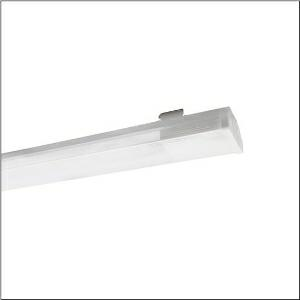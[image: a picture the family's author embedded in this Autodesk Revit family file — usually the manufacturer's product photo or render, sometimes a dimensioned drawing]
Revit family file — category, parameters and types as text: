
# Revit family: modario_r__31_gen_2_53bm8127u4l3d2_2c8d
name_source: partatom
category: Lighting Fixtures
units: mm (PartAtom-declared; Revit-internal decimal feet)

## family parameters
Cut with Voids When Loaded = No
Host = Face
Light Source = No
Part Type = Normal
Room Calculation Point = No
Round Connector Dimension = Use Diameter
Shared = No

## types (1)
- Modario® 31 Gen.2 (1 x LED, 23600 lm, 126 W, 4000K)
    Apparent Load = 126 VA
    CIE Flux Codes = 47 80 95 93 100
    Color Rendering = 80
    Color Temperature = 4000K
    Default Elevation = 1800 mm
    Description = Modario® 31 Gen.2, luminaire insert, of sheet steel, coil coated, white, length: 2.392mm, width: 81mm, height: 82mm, 8x system unit, system units: 299mm, LED rated luminous flux: 23.600lm, light colour: 840, control gear: ON/OFF, with plug, 3-pole, with phase selection, mains connection: 220..240V, AC, 50/60Hz, rated input power: 126W, through-wiring accessed according to module size, primary optical cover: cover, of PMMA, light emission: direct distribution, primary light characteristic: symmetric, protection rating (complete): IP20, protection rating (LED compartment): IP50, insulation class (complete): insulation class I (protective earthing), certification: CE, ENEC, VDE, UKCA, impact resistance: IK03, permissible ambient temperature for indoor applications: -40..+35°C, corresponds to IFS (International Featured Standards) requirements for safety and quality in the food industry, reducing of maximum allowable ambient temperature of 5°C with ceiling mounting, packaging unit: 1 piece
    Height = 92 mm
    Lamp = 1 x LED
    Lamp Light Flux = 23600 lm
    Lamp Power = 126 W
    Lamp count = 1
    Length = 2392 mm
    Luminous efficacy = 187 lm/W
    Manufacturer = Siteco
    ModVariant = No
    Model = 53BM8127U4L3D2
    Mounting Place = Ceiling
    Mounting Type = Pendant
    Number of Poles = 1
    OnlyDefault = Yes
    Power Factor = 1
    Product Name = Modario® 31 Gen.2
    Product group = luminaire insert
    ProductGroupID = 902
    Protection Class = Protection class I
    Protection Degree = IP 20
    RLX_Detail_Level = 1
    RLX_Emergency_Light_Flux = 0 lm
    RLX_Emergency_Type = 0
    RLX_Emergency_Type_DB = No
    RlxData = <blob elided: 34353 chars, md5=b4f1677b>
    Socket = socket
    Standby Power = 0 W
    System Light Flux = 23600 lm
    System Power = 126 W
    Type Comments = Product without accessories
    Type Image = l_1341883.jpg
    URL = http://relux.com
    VarID = ---
    Voltage = 0 V
    Weight = 0.00 kg
    Width = 81 mm

## geometry (parser evidence)
native form markers: Blend x4, Sweep x13
no freeform markers — native parametric forms only
